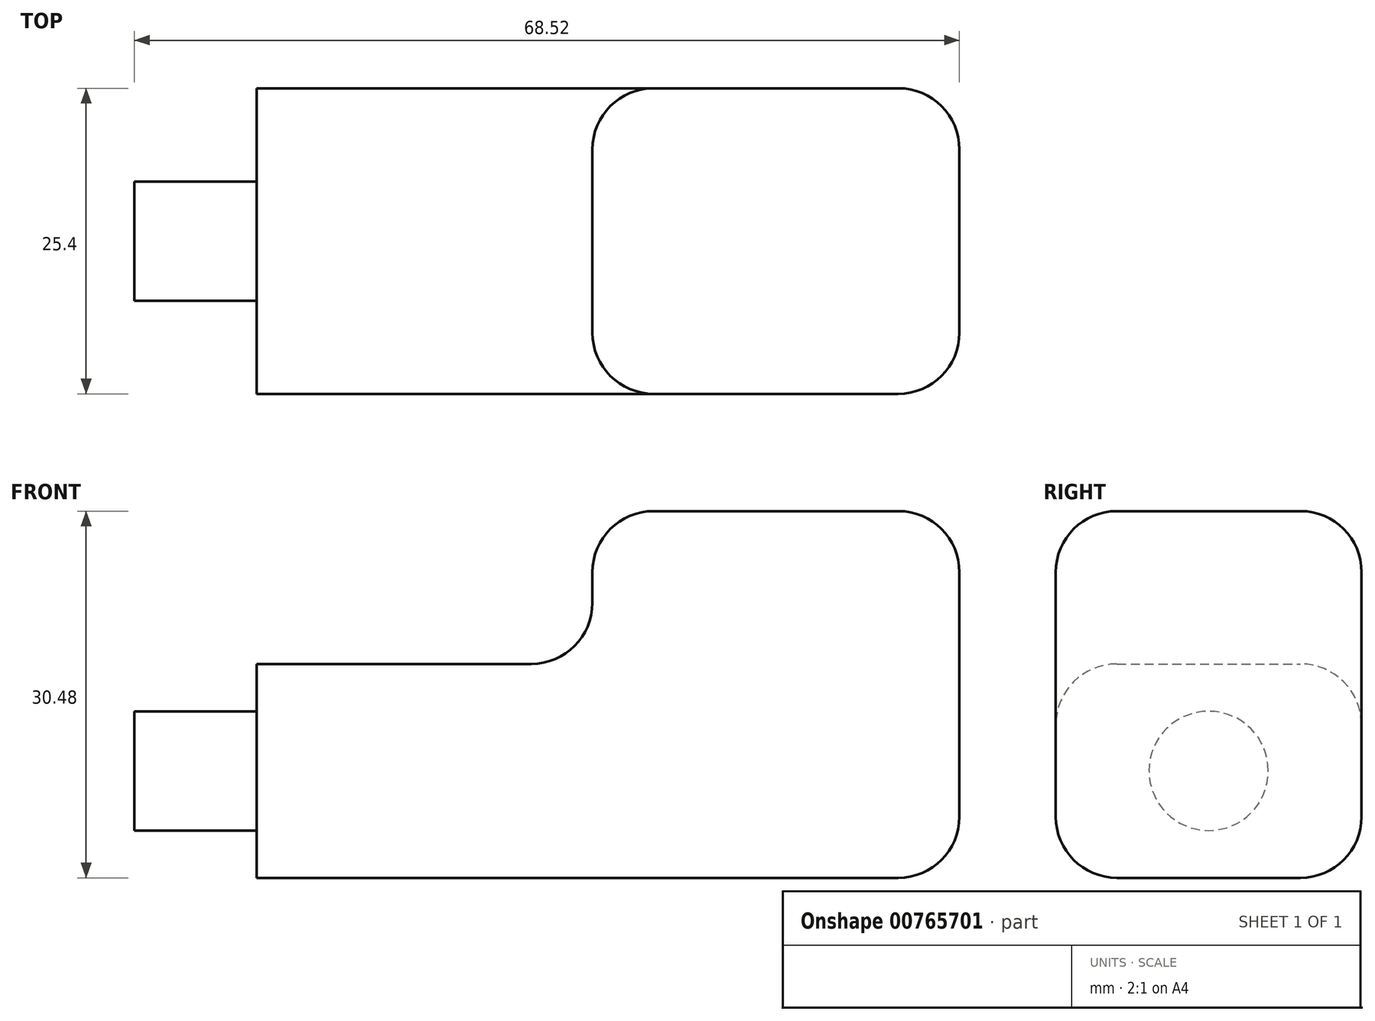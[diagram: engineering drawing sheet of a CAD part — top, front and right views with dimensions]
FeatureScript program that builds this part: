
annotation { "Feature Type Name" : "Feature", "Feature Type Description" : "" }
export const myFeature = defineFeature(function(context is Context, id is Id, definition is map)
    precondition{}
    {
        {
            var Q0;
            Q0=qCreatedBy(makeId("Front.planeOp"),FACE);
            var sketch = newSketch(context, id + "F0", { "sketchPlane" : qUnion([Q0])});
            skLineSegment(sketch, "E0", {"start": v(0, 0) * mm, "end": v(-25.4, 0) * mm});
            skLineSegment(sketch, "E1", {"start": v(17.15, 25.4) * mm, "end": v(16.08, 28.69) * mm});
            skLineSegment(sketch, "E2", {"start": v(25.4, 0) * mm, "end": v(37.57, 0) * mm});
            skLineSegment(sketch, "E3", {"start": v(0, 25.4) * mm, "end": v(-25.4, 25.4) * mm});
            skLineSegment(sketch, "E4", {"start": v(-25.4, 25.4) * mm, "end": v(-33.65, 25.4) * mm});
            skLineSegment(sketch, "E5", {"start": v(25.4, 0) * mm, "end": v(30.48, 0) * mm});
            skLineSegment(sketch, "E6", {"start": v(30.48, 0) * mm, "end": v(30.48, 38.1) * mm});
            skLineSegment(sketch, "E7", {"start": v(0, 25.4) * mm, "end": v(0, 38.08) * mm});
            skLineSegment(sketch, "E8", {"start": v(30.48, 38.1) * mm, "end": v(-12.56, 38.1) * mm});
            skLineSegment(sketch, "E9", {"start": v(0, 38.08) * mm, "end": v(0, 48.33) * mm});
            skLineSegment(sketch, "E10", {"start": v(30.48, 0) * mm, "end": v(30.48, 7.62) * mm});
            skLineSegment(sketch, "E11", {"start": v(30.48, 7.62) * mm, "end": v(-38.73, 7.62) * mm});
            skLineSegment(sketch, "E12", {"start": v(-27.88, 7.62) * mm, "end": v(-27.88, 31.08) * mm});
            skSolve(sketch);
        }
        {
            var Q0;
            {var subQ7=sQuery(id+"F0.wireOp",EDGE,"E3");Q0=makeQuery(id+"F0.imprint","IMPRINT",FACE,{"disambiguationData":[TD([[makeQuery(id+"F0.imprint","IMPRINT",EDGE,{"derivedFrom":subQ7}),1.0]])]});}
            extrude(context, id + "F1", {"entities" : qUnion([Q0]), "depth" : 25.4 * mm, "offsetDistance" : 25.4 * mm});
        }
        {
            var Q0;
            Q0=makeQuery(id+"F1.opExtrude","SWEPT_EDGE",EDGE,{"disambiguationData":[OSD([sQuery(id+"F0.wireOp",EDGE,"E3"),sQuery(id+"F0.wireOp",EDGE,"E7")])]});
            var Q1;
            Q1=makeQuery(id+"F1.opExtrude","SWEPT_EDGE",EDGE,{"disambiguationData":[OSD([sQuery(id+"F0.wireOp",EDGE,"E8"),sQuery(id+"F0.wireOp",EDGE,"E9")])]});
            var Q2;
            Q2=makeQuery(id+"F1.opExtrude","SWEPT_EDGE",EDGE,{"disambiguationData":[OSD([sQuery(id+"F0.wireOp",EDGE,"E6"),sQuery(id+"F0.wireOp",EDGE,"E8")])]});
            var Q3;
            {var subQ0=sQuery(id+"F0.wireOp",EDGE,"E6");Q3=qUnion([makeQuery(id+"F1.opExtrude","SWEPT_EDGE",EDGE,{"disambiguationData":[OSD([subQ0,sQuery(id+"F0.wireOp",EDGE,"E8")])]}),makeQuery(id+"F1.opExtrude","SWEPT_EDGE",EDGE,{"disambiguationData":[OSD([subQ0,sQuery(id+"F0.wireOp",EDGE,"E11")])]})]);}
            fillet(context, id + "F2", {"entities" : qUnion([Q0, Q1, Q2, Q3]), "radius" : 5.08 * mm, "tangentPropagation" : true, "allowEdgeOverflow" : false});
        }
        {
            var Q0;
            Q0=makeQuery(id+"F1.opExtrude","CAP_EDGE",EDGE,{"disambiguationData":[OSD([sQuery(id+"F0.wireOp",EDGE,"E6")])],"isStart":true});
            var Q1;
            Q1=makeQuery(id+"F1.opExtrude","CAP_EDGE",EDGE,{"disambiguationData":[OSD([sQuery(id+"F0.wireOp",EDGE,"E3"),sQuery(id+"F0.wireOp",EDGE,"E4")])],"isStart":false});
            fillet(context, id + "F3", {"entities" : qUnion([Q0, Q1]), "radius" : 5.08 * mm, "tangentPropagation" : true, "allowEdgeOverflow" : false});
        }
        {
            var Q0;
            Q0=makeQuery(id+"F1.opExtrude","SWEPT_FACE",FACE,{"disambiguationData":[OSD([sQuery(id+"F0.wireOp",EDGE,"E12")])]});
            var sketch = newSketch(context, id + "F4", { "sketchPlane" : qUnion([Q0])});
            skLineSegment(sketch, "E13", {"start": v(12.7, 25.4) * mm, "end": v(12.7, 7.62) * mm});
            skCircle(sketch, "E14", {"center": v(12.7, 16.51) * mm, "radius": 4.95 * mm});
            skSolve(sketch);
        }
        {
            var Q0;
            {var subQ0=sQuery(id+"F4.wireOp",EDGE,"E14");var subQ1=sQuery(id+"F4.wireOp",EDGE,"E13");var subQ2=makeQuery(id+"F4.imprint","INTERSECT",VERTEX,{"disambiguationData":[OD(0.0)],"derivedFrom":[subQ1,subQ0]});Q0=makeQuery(id+"F4.imprint","IMPRINT",FACE,{"disambiguationData":[TD([[makeQuery(id+"F4.imprint","IMPRINT",EDGE,{"disambiguationData":[TD([[subQ2,-1.0]])],"derivedFrom":subQ1}),-1.0]])]});}
            var Q1;
            {var subQ0=sQuery(id+"F4.wireOp",EDGE,"E14");var subQ1=sQuery(id+"F4.wireOp",EDGE,"E13");var subQ2=makeQuery(id+"F4.imprint","INTERSECT",VERTEX,{"disambiguationData":[OD(0.0)],"derivedFrom":[subQ1,subQ0]});Q1=makeQuery(id+"F4.imprint","IMPRINT",FACE,{"disambiguationData":[TD([[makeQuery(id+"F4.imprint","IMPRINT",EDGE,{"disambiguationData":[TD([[subQ2,-1.0]])],"derivedFrom":subQ1}),1.0]])]});}
            extrude(context, id + "F5", {"entities" : qUnion([Q0, Q1]), "operationType" : NewBodyOperationType.ADD, "depth" : 10.16 * mm, "offsetDistance" : 25.4 * mm});
        }
    });
